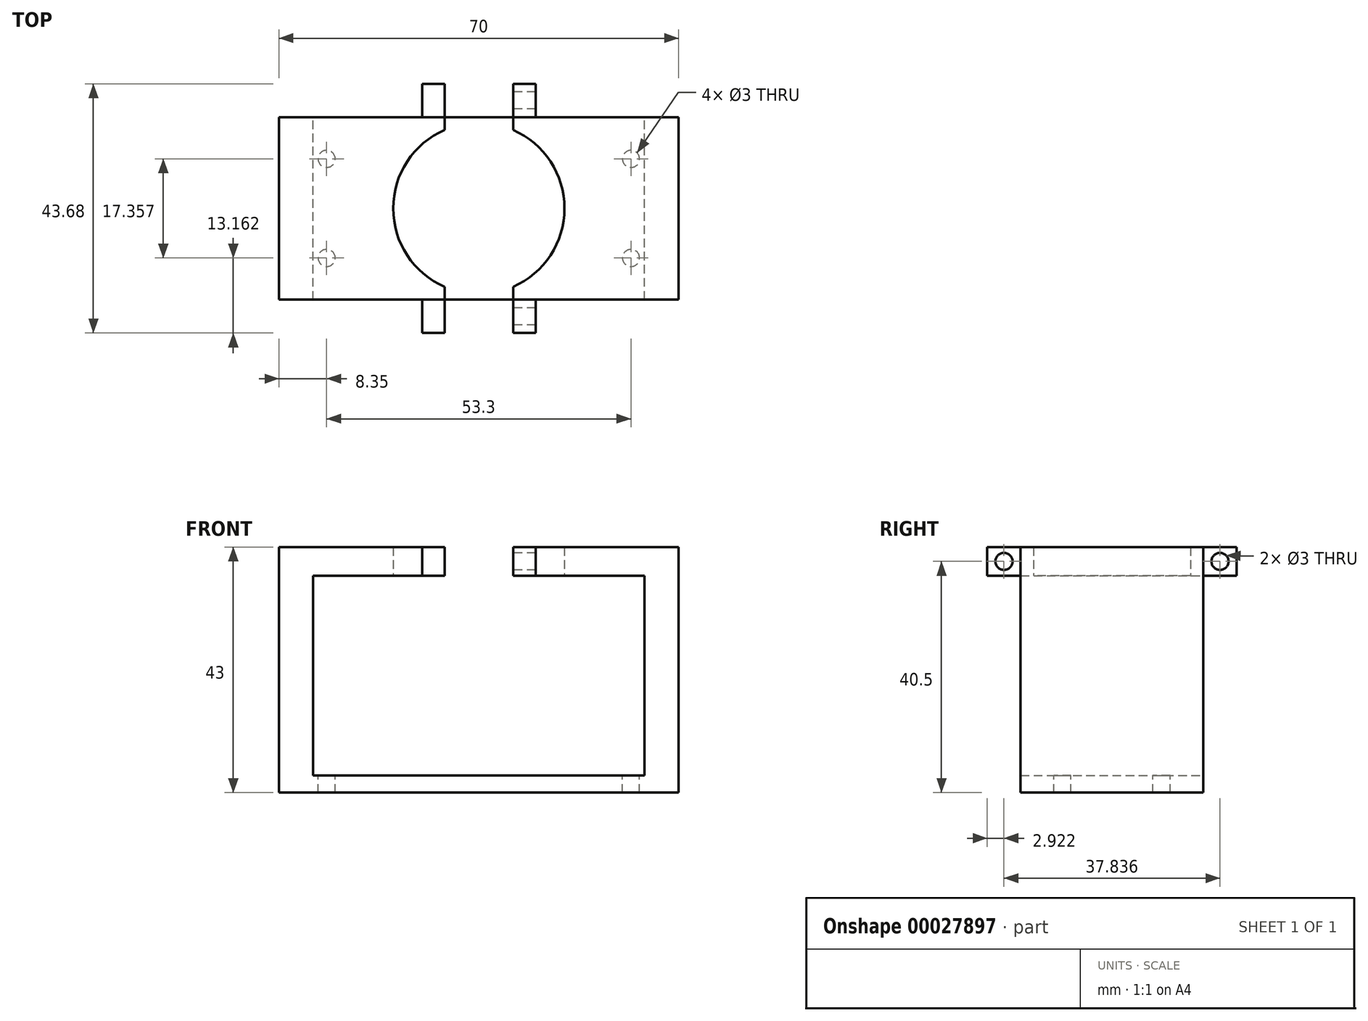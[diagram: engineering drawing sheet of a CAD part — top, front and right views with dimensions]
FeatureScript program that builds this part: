
annotation { "Feature Type Name" : "Feature", "Feature Type Description" : "" }
export const myFeature = defineFeature(function(context is Context, id is Id, definition is map)
    precondition{}
    {
        {
            var Q0;
            Q0=qCreatedBy(makeId("Front.planeOp"),FACE);
            var sketch = newSketch(context, id + "F0", { "sketchPlane" : qUnion([Q0])});
            skLineSegment(sketch, "E0.left", {"start": v(-35, 10.03) * mm, "end": v(-35, 0) * mm});
            skLineSegment(sketch, "E1.top", {"start": v(-35, 40) * mm, "end": v(0, 40) * mm});
            skLineSegment(sketch, "E1.left", {"start": v(-35, 10.03) * mm, "end": v(-35, 40) * mm});
            skLineSegment(sketch, "E2.MirrorCS", {"start": v(35, 40) * mm, "end": v(0, 40) * mm});
            skLineSegment(sketch, "E3.MirrorCS", {"start": v(35, 10.03) * mm, "end": v(35, 40) * mm});
            skLineSegment(sketch, "E4.MirrorCS", {"start": v(35, 10.03) * mm, "end": v(35, 0) * mm});
            skPoint(sketch, "E5.orphan", {"position": v(35, 10.03) * mm});
            skLineSegment(sketch, "E6.right", {"start": v(-29, 10.03) * mm, "end": v(-29, 0) * mm});
            skLineSegment(sketch, "E7.right", {"start": v(29, 10.03) * mm, "end": v(29, 0) * mm});
            skLineSegment(sketch, "E8", {"start": v(29, 0) * mm, "end": v(29, 35) * mm});
            skLineSegment(sketch, "E9", {"start": v(29, 35) * mm, "end": v(-29, 35) * mm});
            skLineSegment(sketch, "E10", {"start": v(-29, 35) * mm, "end": v(-29, 10.03) * mm});
            skLineSegment(sketch, "E11.top", {"start": v(-35, -3) * mm, "end": v(35, -3) * mm});
            skLineSegment(sketch, "E11.left", {"start": v(-35, 0) * mm, "end": v(-35, -3) * mm});
            skLineSegment(sketch, "E11.right", {"start": v(35, 0) * mm, "end": v(35, -3) * mm});
            skLineSegment(sketch, "E12", {"start": v(-29, 0) * mm, "end": v(29, 0) * mm});
            skSolve(sketch);
        }
        {
            var Q0;
            Q0 = qSketchRegion(id + "F0", true);
            extrude(context, id + "F1", {"entities" : qUnion([Q0]), "depth" : 32 * mm});
        }
        {
            var Q0;
            Q0=qCreatedBy(makeId("Top.planeOp"),FACE);
            var sketch = newSketch(context, id + "F2", { "sketchPlane" : qUnion([Q0])});
            skLineSegment(sketch, "E13", {"start": v(0, -32) * mm, "end": v(0, -16) * mm, "construction": true});
            skLineSegment(sketch, "E14", {"start": v(0, -16) * mm, "end": v(26.65, -16) * mm, "construction": true});
            skCircle(sketch, "E15", {"center": v(26.65, -24.68) * mm, "radius": 1.5 * mm});
            skCircle(sketch, "E16.MirrorC", {"center": v(26.65, -7.32) * mm, "radius": 1.5 * mm});
            skCircle(sketch, "E17.MirrorC", {"center": v(-26.65, -24.68) * mm, "radius": 1.5 * mm});
            skCircle(sketch, "E18.MirrorC", {"center": v(-26.65, -7.32) * mm, "radius": 1.5 * mm});
            skPoint(sketch, "E19.right.end.orphan", {"position": v(35, -32) * mm});
            skSolve(sketch);
        }
        {
            var Q0;
            Q0 = qSketchRegion(id + "F2", true);
            extrude(context, id + "F3", {"entities" : qUnion([Q0]), "operationType" : NewBodyOperationType.REMOVE, "oppositeDirection" : true, "depth" : 25 * mm});
        }
        {
            var Q0;
            Q0=qCreatedBy(makeId("Top.planeOp"),FACE);
            var sketch = newSketch(context, id + "F4", { "sketchPlane" : qUnion([Q0])});
            skLineSegment(sketch, "E20.rect.bottom", {"start": v(6, -32) * mm, "end": v(-6, -32) * mm});
            skLineSegment(sketch, "E20.rect.top", {"start": v(6, 0) * mm, "end": v(-6, 0) * mm});
            skLineSegment(sketch, "E20.rect.left", {"start": v(6, -32) * mm, "end": v(6, 0) * mm});
            skLineSegment(sketch, "E20.rect.right", {"start": v(-6, -32) * mm, "end": v(-6, 0) * mm});
            skPoint(sketch, "E20.rect.middle", {"position": v(0, -16) * mm});
            skSolve(sketch);
        }
        {
            var Q0;
            Q0 = qSketchRegion(id + "F4", true);
            extrude(context, id + "F5", {"entities" : qUnion([Q0]), "operationType" : NewBodyOperationType.REMOVE, "depth" : 58.4 * mm});
        }
        {
            var Q0;
            Q0=qCreatedBy(makeId("Top.planeOp"),FACE);
            var sketch = newSketch(context, id + "F6", { "sketchPlane" : qUnion([Q0])});
            skLineSegment(sketch, "E21.bottom", {"start": v(-6, 0) * mm, "end": v(-9.93, 0) * mm});
            skLineSegment(sketch, "E21.left", {"start": v(-6, 0) * mm, "end": v(-6, 5.84) * mm});
            skLineSegment(sketch, "E22.MirrorCS", {"start": v(6, 0) * mm, "end": v(6, 5.84) * mm});
            skLineSegment(sketch, "E23.MirrorCS", {"start": v(6, 0) * mm, "end": v(9.93, 0) * mm});
            skLineSegment(sketch, "E24", {"start": v(0, 0) * mm, "end": v(0, -16) * mm, "construction": true});
            skLineSegment(sketch, "E25", {"start": v(0, -16) * mm, "end": v(23.07, -16) * mm, "construction": true});
            skLineSegment(sketch, "E26", {"start": v(23.07, -16) * mm, "end": v(-21.68, -16) * mm, "construction": true});
            skLineSegment(sketch, "E27.MirrorCS", {"start": v(-6, -32) * mm, "end": v(-6, -37.84) * mm});
            skLineSegment(sketch, "E28.MirrorCS", {"start": v(-6, -32) * mm, "end": v(-9.93, -32) * mm});
            skLineSegment(sketch, "E29.MirrorCS", {"start": v(6, -32) * mm, "end": v(6, -37.84) * mm});
            skLineSegment(sketch, "E30.MirrorCS", {"start": v(6, -32) * mm, "end": v(9.93, -32) * mm});
            skLineSegment(sketch, "E31.top", {"start": v(-6, 5.84) * mm, "end": v(-9.93, 5.84) * mm});
            skLineSegment(sketch, "E31.right", {"start": v(-9.93, 0) * mm, "end": v(-9.93, 5.84) * mm});
            skLineSegment(sketch, "E32", {"start": v(9.93, 0) * mm, "end": v(9.93, 5.84) * mm});
            skLineSegment(sketch, "E33", {"start": v(9.93, 5.84) * mm, "end": v(6, 5.84) * mm});
            skLineSegment(sketch, "E34", {"start": v(-9.93, -32) * mm, "end": v(-9.93, -37.84) * mm});
            skLineSegment(sketch, "E35", {"start": v(-9.93, -37.84) * mm, "end": v(-6, -37.84) * mm});
            skLineSegment(sketch, "E36", {"start": v(6, -37.84) * mm, "end": v(9.93, -37.84) * mm});
            skLineSegment(sketch, "E37", {"start": v(9.93, -37.84) * mm, "end": v(9.93, -32) * mm});
            skPoint(sketch, "E38.MirrorCS.end.orphan", {"position": v(9.93, -32) * mm});
            skPoint(sketch, "E38.MirrorCS.start.orphan", {"position": v(6, -37.84) * mm});
            skPoint(sketch, "E39.MirrorCS.start.orphan", {"position": v(-6, -37.84) * mm});
            skPoint(sketch, "E40.MirrorCS.start.orphan", {"position": v(6, 5.84) * mm});
            skSolve(sketch);
        }
        {
            var Q0;
            Q0 = qSketchRegion(id + "F6", true);
            extrude(context, id + "F7", {"entities" : qUnion([Q0]), "depth" : 40 * mm, "hasSecondDirection" : true, "secondDirectionOppositeDirection" : false, "secondDirectionDepth" : 35 * mm});
        }
        {
            var Q0;
            Q0=qCreatedBy(makeId("Right.planeOp"),FACE);
            var sketch = newSketch(context, id + "F8", { "sketchPlane" : qUnion([Q0])});
            skCircle(sketch, "E41", {"center": v(2.92, 37.5) * mm, "radius": 1.5 * mm});
            skLineSegment(sketch, "E42", {"start": v(0, 40.11) * mm, "end": v(-16, 40.11) * mm, "construction": true});
            skLineSegment(sketch, "E43", {"start": v(-16, 40.11) * mm, "end": v(-16, 33.3) * mm, "construction": true});
            skCircle(sketch, "E44.MirrorC", {"center": v(-34.92, 37.5) * mm, "radius": 1.5 * mm});
            skSolve(sketch);
        }
        {
            var Q0;
            Q0 = qSketchRegion(id + "F8", true);
            extrude(context, id + "F9", {"entities" : qUnion([Q0]), "operationType" : NewBodyOperationType.REMOVE, "depth" : 25 * mm});
        }
        {
            var Q0;
            Q0=qCreatedBy(makeId("Top.planeOp"),FACE);
            var sketch = newSketch(context, id + "F10", { "sketchPlane" : qUnion([Q0])});
            skLineSegment(sketch, "E45", {"start": v(0, 0) * mm, "end": v(0, -16) * mm, "construction": true});
            skCircle(sketch, "E46", {"center": v(0, -16) * mm, "radius": 15 * mm});
            skSolve(sketch);
        }
        {
            var Q0;
            Q0 = qSketchRegion(id + "F10", true);
            extrude(context, id + "F11", {"entities" : qUnion([Q0]), "operationType" : NewBodyOperationType.REMOVE, "depth" : 76.8 * mm});
        }
    });
